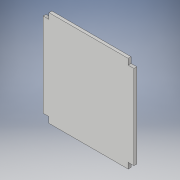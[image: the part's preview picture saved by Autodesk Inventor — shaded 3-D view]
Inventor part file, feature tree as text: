
AUTODESK INVENTOR PART (.ipt)
format: ipt  version: 2018 (Build 220112000, 112)  size: 102,912 bytes
history: native  units: in
note: dims shown in document units (in); Inventor stores cm internally (conversion verified against a paired STEP export)
features: extrude x1, sketch x1
ambient origin geometry x8: Origin, YZ Plane, XZ Plane, XY Plane, X Axis, Y Axis, Z Axis, Center Point
bodies: Solid1 (feature_tree)
feature tree (2):
  extrude  "Extrusion1"  Depth=2.0in
  sketch  "Sketch1"  dims[d0=27.262in d1=2.0in d2=2.0in d3=29.0in d4=2.0in d5=2.0in d6=2.0in d7=2.0in d8=1.0in d9=0.0in]
